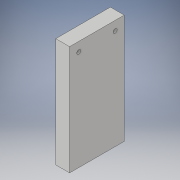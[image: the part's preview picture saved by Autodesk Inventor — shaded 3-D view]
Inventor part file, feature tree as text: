
AUTODESK INVENTOR PART (.ipt)
format: ipt  version: 2019 (Build 230136000, 136)  size: 102,400 bytes
history: native  units: in
note: dims shown in document units (in); Inventor stores cm internally (conversion verified against a paired STEP export)
features: sketch x2, extrude x1, hole x1
ambient origin geometry x8: Origin, YZ Plane, XZ Plane, XY Plane, X Axis, Y Axis, Z Axis, Center Point
bodies: Solid1 (feature_tree)
feature tree (4):
  extrude  "Extrusion1"  Depth=1.5in
  hole  "Hole1"  [1 undecoded]
  sketch  "Sketch1"  dims[d0=0.38in d1=1.5in]
  sketch  "Sketch2"  dims[d2=3.0in d3=0.0in d4=0.25in d5=0.25in d6=0.25in d7=0.25in d8=0.107in d9=0.75in d10=0.375in d11=0.25in d12=0.5635in d13=1.0in d14=0.8108in]
note: 1 required parameter value undecoded (feature->parameter linkage not recoverable at this tier; creation-order binding heuristic only, values carry confidence <= 0.55)
